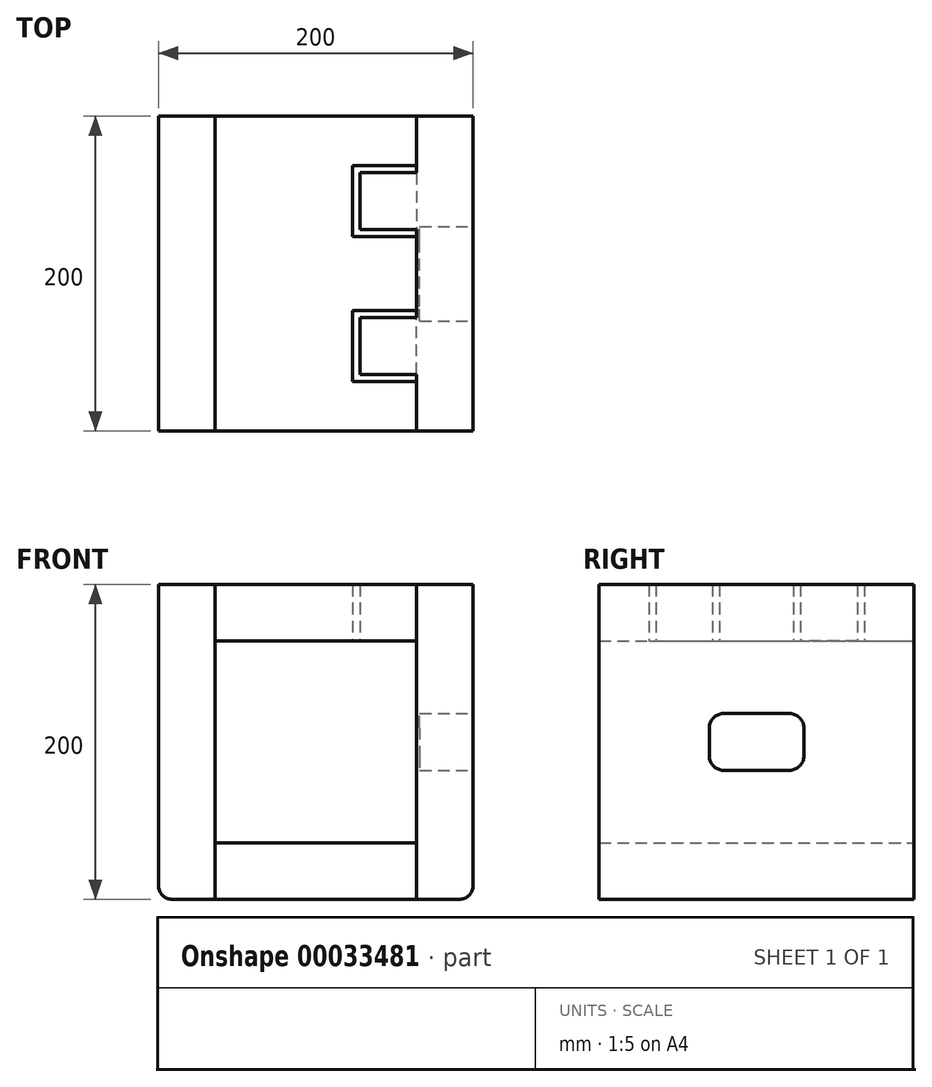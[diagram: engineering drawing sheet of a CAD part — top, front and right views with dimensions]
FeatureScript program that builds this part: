
annotation { "Feature Type Name" : "Feature", "Feature Type Description" : "" }
export const myFeature = defineFeature(function(context is Context, id is Id, definition is map)
    precondition{}
    {
        {
            assignVariable(context, id + "F0", {"name" : "MDF", "anyValue" : 36});
        }
        {
            var Q0;
            Q0=qCreatedBy(makeId("Front.planeOp"),FACE);
            var sketch = newSketch(context, id + "F1", { "sketchPlane" : qUnion([Q0])});
            skLineSegment(sketch, "E0.bottom", {"start": v(-96.88, 111.45) * mm, "end": v(-60.88, 111.45) * mm});
            skLineSegment(sketch, "E0.top", {"start": v(-96.88, -88.55) * mm, "end": v(-60.88, -88.55) * mm});
            skLineSegment(sketch, "E0.left", {"start": v(-96.88, 111.45) * mm, "end": v(-96.88, -88.55) * mm});
            skLineSegment(sketch, "E0.right", {"start": v(-60.88, 111.45) * mm, "end": v(-60.88, -52.55) * mm});
            skLineSegment(sketch, "E1.bottom", {"start": v(-60.88, 111.45) * mm, "end": v(67.12, 111.45) * mm});
            skLineSegment(sketch, "E1.top", {"start": v(-60.88, 75.45) * mm, "end": v(67.12, 75.45) * mm});
            skLineSegment(sketch, "E1.left", {"start": v(-60.88, 111.45) * mm, "end": v(-60.88, 75.45) * mm});
            skLineSegment(sketch, "E1.right", {"start": v(67.12, 111.45) * mm, "end": v(67.12, 75.45) * mm});
            skLineSegment(sketch, "E2.bottom", {"start": v(67.12, 111.45) * mm, "end": v(103.12, 111.45) * mm});
            skLineSegment(sketch, "E2.top", {"start": v(67.12, -88.55) * mm, "end": v(103.12, -88.55) * mm});
            skLineSegment(sketch, "E2.left", {"start": v(67.12, 111.45) * mm, "end": v(67.12, -88.55) * mm});
            skLineSegment(sketch, "E2.right", {"start": v(103.12, 111.45) * mm, "end": v(103.12, -88.55) * mm});
            skLineSegment(sketch, "E3.bottom", {"start": v(-60.88, -52.55) * mm, "end": v(67.12, -52.55) * mm});
            skLineSegment(sketch, "E3.top", {"start": v(-60.88, -88.55) * mm, "end": v(67.12, -88.55) * mm});
            skLineSegment(sketch, "E3.left", {"start": v(-60.88, -52.55) * mm, "end": v(-60.88, -88.55) * mm});
            skLineSegment(sketch, "E3.right", {"start": v(67.12, -52.55) * mm, "end": v(67.12, -88.55) * mm});
            skSolve(sketch);
        }
        {
            var Q0;
            Q0=makeQuery(id+"F1.imprint","IMPRINT",FACE,{"disambiguationData":[TD([[makeQuery(id+"F1.imprint","IMPRINT",EDGE,{"derivedFrom":sQuery(id+"F1.wireOp",EDGE,"E0.bottom")}),-1.0]])]});
            var Q1;
            {var subQ3=sQuery(id+"F1.wireOp",EDGE,"E2.bottom");Q1=makeQuery(id+"F1.imprint","IMPRINT",FACE,{"disambiguationData":[TD([[makeQuery(id+"F1.imprint","IMPRINT",EDGE,{"derivedFrom":subQ3}),-1.0]])]});}
            extrude(context, id + "F2", {"entities" : qUnion([Q0, Q1]), "depth" : 200 * mm});
        }
        {
            var Q0;
            {var subQ2=sQuery(id+"F1.wireOp",EDGE,"E1.bottom");Q0=makeQuery(id+"F1.imprint","IMPRINT",FACE,{"disambiguationData":[TD([[makeQuery(id+"F1.imprint","IMPRINT",EDGE,{"derivedFrom":subQ2}),-1.0]])]});}
            var Q1;
            Q1=makeQuery(id+"F1.imprint","IMPRINT",FACE,{"disambiguationData":[TD([[makeQuery(id+"F1.imprint","IMPRINT",EDGE,{"derivedFrom":sQuery(id+"F1.wireOp",EDGE,"E3.bottom")}),-1.0]])]});
            extrude(context, id + "F3", {"entities" : qUnion([Q0, Q1]), "depth" : 200 * mm});
        }
        {
            var Q0;
            Q0=makeQuery(id+"F2.opExtrude","SWEPT_FACE",FACE,{"disambiguationData":[OSD([sQuery(id+"F1.wireOp",EDGE,"E2.right")])]});
            var sketch = newSketch(context, id + "F4", { "sketchPlane" : qUnion([Q0])});
            skLineSegment(sketch, "E4.bottom", {"start": v(-200, 111.45) * mm, "end": v(0, 111.45) * mm});
            skLineSegment(sketch, "E4.top", {"start": v(-200, -88.55) * mm, "end": v(0, -88.55) * mm});
            skLineSegment(sketch, "E4.left", {"start": v(-200, 111.45) * mm, "end": v(-200, -88.55) * mm});
            skLineSegment(sketch, "E4.right", {"start": v(0, 111.45) * mm, "end": v(0, -88.55) * mm});
            skLineSegment(sketch, "E5.rect.bottom", {"start": v(-130, 29.45) * mm, "end": v(-70, 29.45) * mm});
            skLineSegment(sketch, "E5.rect.top", {"start": v(-130, -6.55) * mm, "end": v(-70, -6.55) * mm});
            skLineSegment(sketch, "E5.rect.left", {"start": v(-130, 29.45) * mm, "end": v(-130, -6.55) * mm});
            skLineSegment(sketch, "E5.rect.right", {"start": v(-70, 29.45) * mm, "end": v(-70, -6.55) * mm});
            skPoint(sketch, "E5.rect.middle", {"position": v(-100, 11.45) * mm});
            skPoint(sketch, "E5.rect.middle.positionSnap1", {"position": v(-200, 11.45) * mm});
            skPoint(sketch, "E5.rect.centerSnap1", {"position": v(-200, 11.45) * mm});
            skSolve(sketch);
        }
        {
            var Q0;
            Q0=makeQuery(id+"F4.imprint","IMPRINT",FACE,{"disambiguationData":[TD([[makeQuery(id+"F4.imprint","IMPRINT",EDGE,{"derivedFrom":sQuery(id+"F4.wireOp",EDGE,"E5.rect.bottom")}),-1.0]])]});
            extrude(context, id + "F5", {"entities" : qUnion([Q0]), "operationType" : NewBodyOperationType.REMOVE, "oppositeDirection" : true, "depth" : (getVariable(context, 'MDF') - 2) * mm});
        }
        {
            var Q0;
            Q0=makeQuery(id+"F5.boolean.opBoolean","COPY",EDGE,{"derivedFrom":makeQuery(id+"F5.opExtrude","SWEPT_EDGE",EDGE,{"disambiguationData":[OSD([sQuery(id+"F4.wireOp",EDGE,"E5.rect.bottom"),sQuery(id+"F4.wireOp",EDGE,"E5.rect.left")])]})});
            var Q1;
            Q1=makeQuery(id+"F5.boolean.opBoolean","COPY",EDGE,{"derivedFrom":makeQuery(id+"F5.opExtrude","SWEPT_EDGE",EDGE,{"disambiguationData":[OSD([sQuery(id+"F4.wireOp",EDGE,"E5.rect.bottom"),sQuery(id+"F4.wireOp",EDGE,"E5.rect.right")])]})});
            var Q2;
            Q2=makeQuery(id+"F5.boolean.opBoolean","COPY",EDGE,{"derivedFrom":makeQuery(id+"F5.opExtrude","SWEPT_EDGE",EDGE,{"disambiguationData":[OSD([sQuery(id+"F4.wireOp",EDGE,"E5.rect.top"),sQuery(id+"F4.wireOp",EDGE,"E5.rect.right")])]})});
            var Q3;
            Q3=makeQuery(id+"F5.boolean.opBoolean","COPY",EDGE,{"derivedFrom":makeQuery(id+"F5.opExtrude","SWEPT_EDGE",EDGE,{"disambiguationData":[OSD([sQuery(id+"F4.wireOp",EDGE,"E5.rect.top"),sQuery(id+"F4.wireOp",EDGE,"E5.rect.left")])]})});
            fillet(context, id + "F6", {"entities" : qUnion([Q0, Q1, Q2, Q3]), "radius" : (getVariable(context, 'MDF') / 4) * mm, "tangentPropagation" : true, "allowEdgeOverflow" : false});
        }
        {
            var Q0;
            Q0=makeQuery(id+"F2.opExtrude","SWEPT_FACE",FACE,{"disambiguationData":[OSD([sQuery(id+"F1.wireOp",EDGE,"E2.right")])]});
            var sketch = newSketch(context, id + "F7", { "sketchPlane" : qUnion([Q0])});
            skLineSegment(sketch, "E6.bottom", {"start": v(-164, 111.45) * mm, "end": v(-128, 111.45) * mm});
            skLineSegment(sketch, "E6.top", {"start": v(-164, 75.45) * mm, "end": v(-128, 75.45) * mm});
            skLineSegment(sketch, "E6.left", {"start": v(-164, 111.45) * mm, "end": v(-164, 75.45) * mm});
            skLineSegment(sketch, "E6.right", {"start": v(-128, 111.45) * mm, "end": v(-128, 75.45) * mm});
            skLineSegment(sketch, "E7.bottom", {"start": v(-36, 111.45) * mm, "end": v(-72, 111.45) * mm});
            skLineSegment(sketch, "E7.top", {"start": v(-36, 75.45) * mm, "end": v(-72, 75.45) * mm});
            skLineSegment(sketch, "E7.left", {"start": v(-36, 111.45) * mm, "end": v(-36, 75.45) * mm});
            skLineSegment(sketch, "E7.right", {"start": v(-72, 111.45) * mm, "end": v(-72, 75.45) * mm});
            skSolve(sketch);
        }
        {
            var Q0;
            Q0=makeQuery(id+"F7.imprint","IMPRINT",FACE,{"disambiguationData":[TD([[makeQuery(id+"F7.imprint","IMPRINT",EDGE,{"derivedFrom":sQuery(id+"F7.wireOp",EDGE,"E7.bottom")}),-1.0]])]});
            var Q1;
            Q1=makeQuery(id+"F7.imprint","IMPRINT",FACE,{"disambiguationData":[TD([[makeQuery(id+"F7.imprint","IMPRINT",EDGE,{"derivedFrom":sQuery(id+"F7.wireOp",EDGE,"E6.bottom")}),-1.0]])]});
            extrude(context, id + "F8", {"entities" : qUnion([Q0, Q1]), "oppositeDirection" : true, "depth" : (getVariable(context, 'MDF') * 2) * mm});
        }
        {
            var Q0;
            Q0=makeQuery(id+"F8.opExtrude","SWEPT_BODY",BODY,{"disambiguationData":[OSD([sQuery(id+"F7.wireOp",EDGE,"E6.bottom"),sQuery(id+"F7.wireOp",EDGE,"E6.top"),sQuery(id+"F7.wireOp",EDGE,"E6.left"),sQuery(id+"F7.wireOp",EDGE,"E6.right")])]});
            var Q1;
            Q1=makeQuery(id+"F8.opExtrude","SWEPT_BODY",BODY,{"disambiguationData":[OSD([sQuery(id+"F7.wireOp",EDGE,"E7.bottom"),sQuery(id+"F7.wireOp",EDGE,"E7.top"),sQuery(id+"F7.wireOp",EDGE,"E7.left"),sQuery(id+"F7.wireOp",EDGE,"E7.right")])]});
            var Q2;
            Q2=makeQuery(id+"F3.opExtrude","SWEPT_BODY",BODY,{"disambiguationData":[OSD([sQuery(id+"F1.wireOp",EDGE,"E1.bottom"),sQuery(id+"F1.wireOp",EDGE,"E1.top"),sQuery(id+"F1.wireOp",EDGE,"E1.left"),sQuery(id+"F1.wireOp",EDGE,"E2.left")])]});
            booleanBodies(context, id + "F9", {"operationType" : BooleanOperationType.SUBTRACTION, "tools" : qUnion([Q0, Q1]), "targets" : qUnion([Q2]), "offset" : true, "offsetAll" : true, "offsetDistance" : (getVariable(context, 'MDF') / 8) * mm});
        }
        {
            var Q0;
            Q0=makeQuery(id+"F7.imprint","IMPRINT",FACE,{"disambiguationData":[TD([[makeQuery(id+"F7.imprint","IMPRINT",EDGE,{"derivedFrom":sQuery(id+"F7.wireOp",EDGE,"E6.bottom")}),-1.0]])]});
            var Q1;
            Q1=makeQuery(id+"F7.imprint","IMPRINT",FACE,{"disambiguationData":[TD([[makeQuery(id+"F7.imprint","IMPRINT",EDGE,{"derivedFrom":sQuery(id+"F7.wireOp",EDGE,"E7.bottom")}),-1.0]])]});
            extrude(context, id + "F10", {"entities" : qUnion([Q0, Q1]), "operationType" : NewBodyOperationType.ADD, "oppositeDirection" : true, "depth" : (getVariable(context, 'MDF') * 2) * mm});
        }
        {
            var Q0;
            Q0=makeQuery(id+"F2.opExtrude","SWEPT_EDGE",EDGE,{"disambiguationData":[OSD([sQuery(id+"F1.wireOp",EDGE,"E2.top"),sQuery(id+"F1.wireOp",EDGE,"E2.right")])]});
            var Q1;
            Q1=makeQuery(id+"F2.opExtrude","SWEPT_EDGE",EDGE,{"disambiguationData":[OSD([sQuery(id+"F1.wireOp",EDGE,"E0.top"),sQuery(id+"F1.wireOp",EDGE,"E0.left")])]});
            fillet(context, id + "F11", {"entities" : qUnion([Q0, Q1]), "radius" : (getVariable(context, 'MDF') / 4) * mm, "tangentPropagation" : true, "allowEdgeOverflow" : false});
        }
    });
